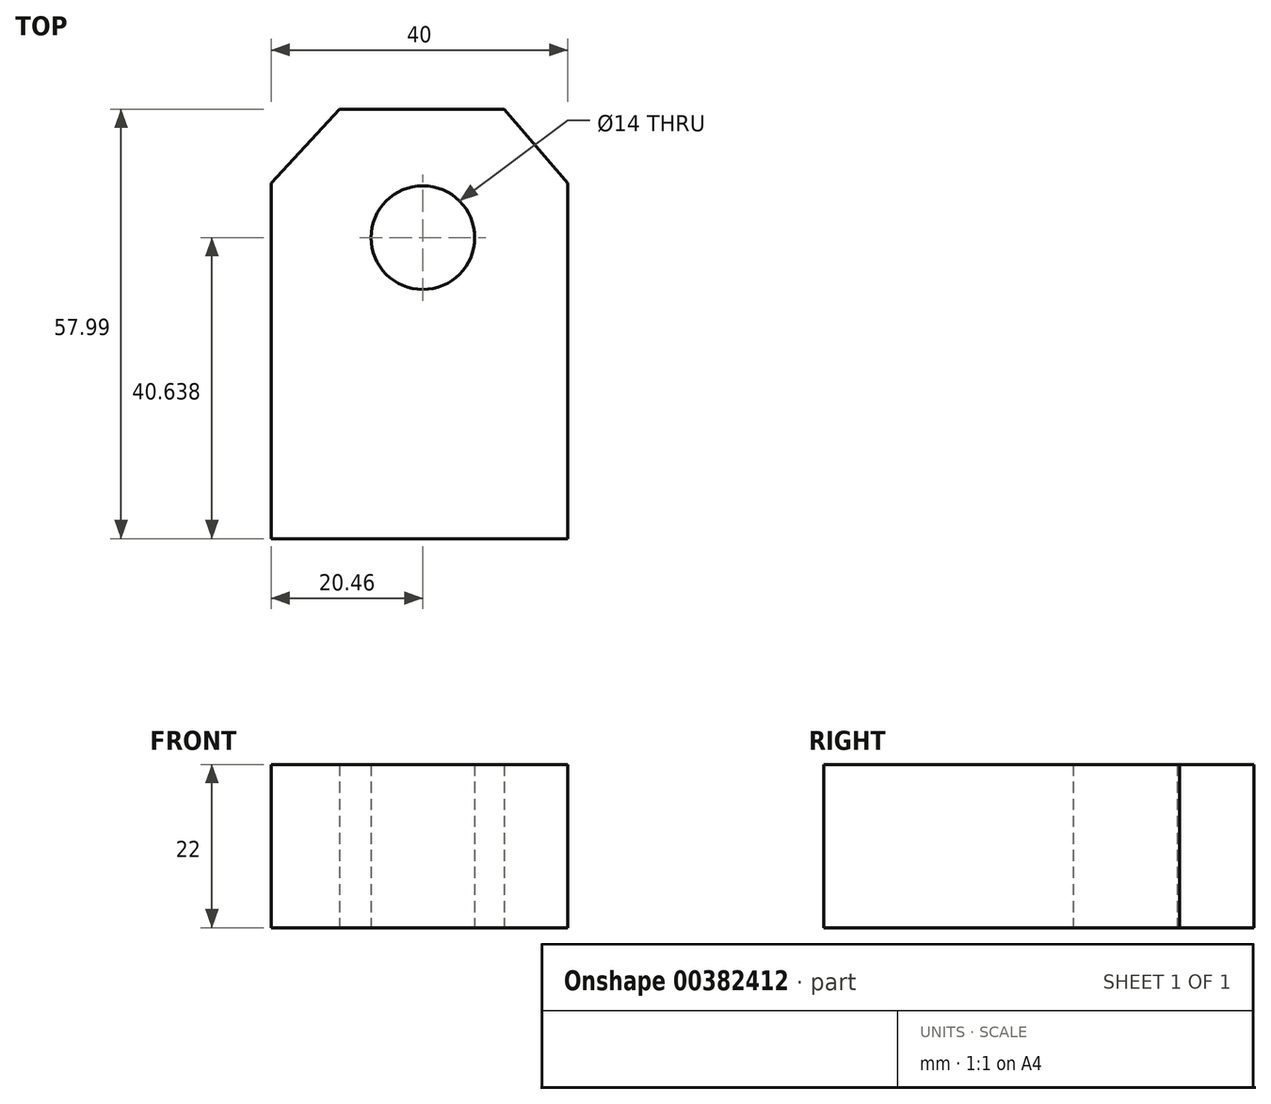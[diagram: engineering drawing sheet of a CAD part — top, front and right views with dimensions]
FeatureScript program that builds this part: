
annotation { "Feature Type Name" : "Feature", "Feature Type Description" : "" }
export const myFeature = defineFeature(function(context is Context, id is Id, definition is map)
    precondition{}
    {
        {
            var Q0;
            Q0=qCreatedBy(makeId("Top.planeOp"),FACE);
            var sketch = newSketch(context, id + "F0", { "sketchPlane" : qUnion([Q0])});
            skLineSegment(sketch, "E0", {"start": v(0, 0) * mm, "end": v(-20.46, 0) * mm});
            skLineSegment(sketch, "E1", {"start": v(-20.46, 0) * mm, "end": v(-20.46, 47.98) * mm});
            skLineSegment(sketch, "E2", {"start": v(-20.46, 47.98) * mm, "end": v(-11.25, 57.99) * mm});
            skLineSegment(sketch, "E3", {"start": v(-11.25, 57.99) * mm, "end": v(10.97, 57.99) * mm});
            skLineSegment(sketch, "E4", {"start": v(10.97, 57.99) * mm, "end": v(19.54, 47.98) * mm});
            skLineSegment(sketch, "E5", {"start": v(19.54, 47.98) * mm, "end": v(19.54, 0) * mm});
            skLineSegment(sketch, "E6", {"start": v(19.54, 0) * mm, "end": v(0, 0) * mm});
            skCircle(sketch, "E7", {"center": v(0, 40.64) * mm, "radius": 7 * mm});
            skSolve(sketch);
        }
        {
            var Q0;
            Q0=makeQuery(id+"F0.imprint","IMPRINT",FACE,{"disambiguationData":[TD([[makeQuery(id+"F0.imprint","IMPRINT",EDGE,{"derivedFrom":sQuery(id+"F0.wireOp",EDGE,"E0")}),-1.0]])]});
            extrude(context, id + "F1", {"entities" : qUnion([Q0]), "depth" : 22 * mm});
        }
    });
